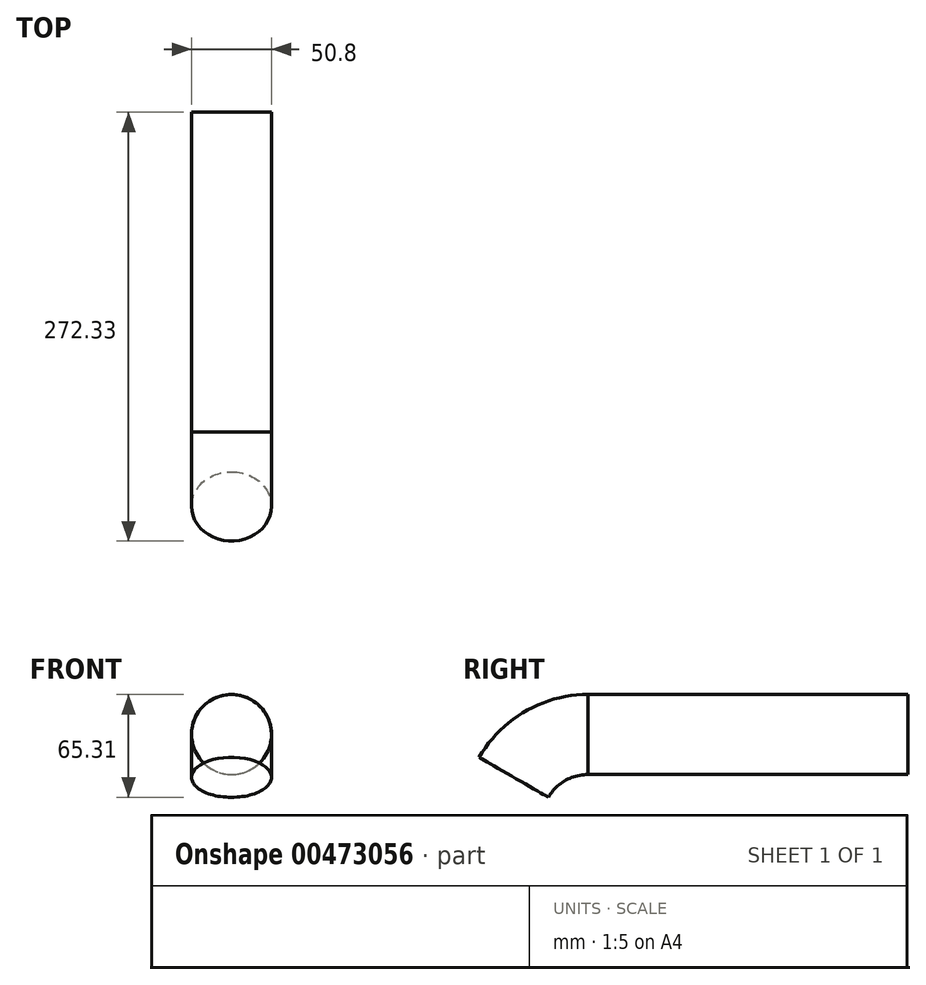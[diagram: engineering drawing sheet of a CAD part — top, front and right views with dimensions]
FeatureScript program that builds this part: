
annotation { "Feature Type Name" : "Feature", "Feature Type Description" : "" }
export const myFeature = defineFeature(function(context is Context, id is Id, definition is map)
    precondition{}
    {
        {
            var Q0;
            Q0=qCreatedBy(makeId("Front.planeOp"),FACE);
            var sketch = newSketch(context, id + "F0", { "sketchPlane" : qUnion([Q0])});
            skCircle(sketch, "E0", {"center": v(0, 0) * mm, "radius": 25.4 * mm});
            skLineSegment(sketch, "E1", {"start": v(0, -54.42) * mm, "end": v(50.42, -54.42) * mm});
            skSolve(sketch);
        }
        {
            var Q0;
            Q0=makeQuery(id+"F0.imprint","IMPRINT",FACE,{"disambiguationData":[TD([[makeQuery(id+"F0.imprint","IMPRINT",EDGE,{"derivedFrom":sQuery(id+"F0.wireOp",EDGE,"E0")}),1.0]])]});
            var Q1;
            Q1=sQuery(id+"F0.wireOp",EDGE,"E1");
            revolve(context, id + "F1", {"entities" : qUnion([Q0]), "axis" : qUnion([Q1]), "revolveType" : RevolveType.ONE_DIRECTION, "angle" : 60 * degree});
        }
        {
            var Q0;
            Q0 = qSketchRegion(id + "F0", true);
            extrude(context, id + "F2", {"entities" : qUnion([Q0]), "oppositeDirection" : true, "depth" : 203.2 * mm});
        }
    });
